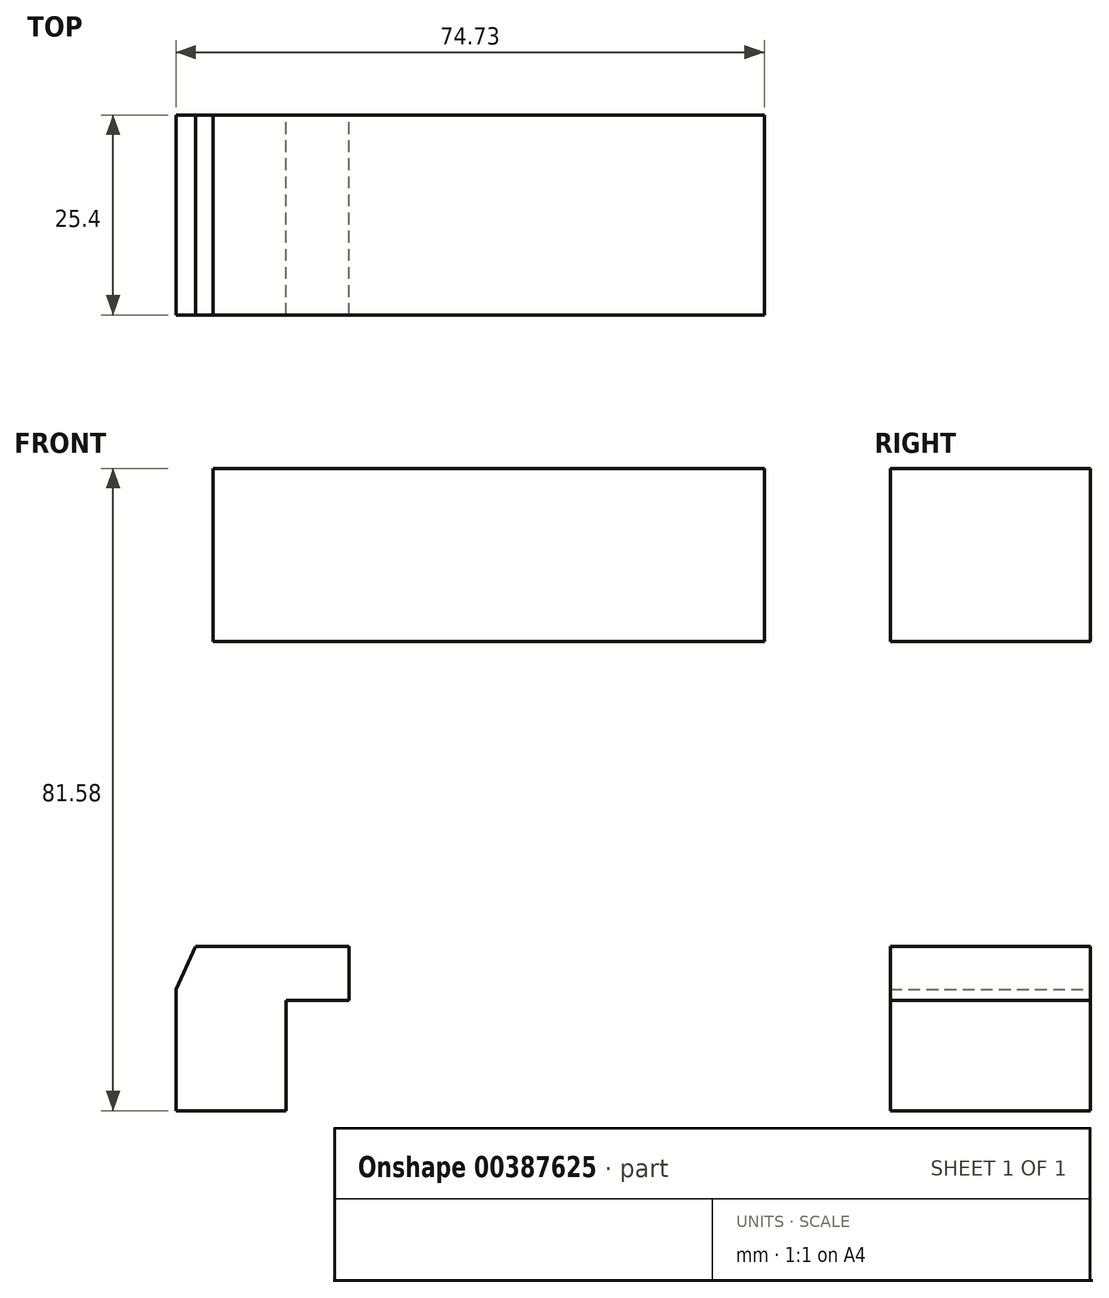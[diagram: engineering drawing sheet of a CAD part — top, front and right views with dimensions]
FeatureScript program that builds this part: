
annotation { "Feature Type Name" : "Feature", "Feature Type Description" : "" }
export const myFeature = defineFeature(function(context is Context, id is Id, definition is map)
    precondition{}
    {
        {
            var Q0;
            Q0=qCreatedBy(makeId("Front.planeOp"),FACE);
            var sketch = newSketch(context, id + "F0", { "sketchPlane" : qUnion([Q0])});
            skLineSegment(sketch, "E0.bottom", {"start": v(-36.75, 49.3) * mm, "end": v(33.26, 49.3) * mm});
            skLineSegment(sketch, "E0.top", {"start": v(-36.75, 27.3) * mm, "end": v(33.26, 27.3) * mm});
            skLineSegment(sketch, "E0.left", {"start": v(-36.75, 49.3) * mm, "end": v(-36.75, 27.3) * mm});
            skLineSegment(sketch, "E0.right", {"start": v(33.26, 49.3) * mm, "end": v(33.26, 27.3) * mm});
            skLineSegment(sketch, "E1.left", {"start": v(-36.75, 49.3) * mm, "end": v(-36.75, 38.3) * mm});
            skLineSegment(sketch, "E1.right", {"start": v(33.26, 49.3) * mm, "end": v(33.26, 38.3) * mm});
            skLineSegment(sketch, "E2", {"start": v(-41.47, -16.9) * mm, "end": v(-41.47, -32.29) * mm});
            skLineSegment(sketch, "E3", {"start": v(-27.48, -32.29) * mm, "end": v(-41.47, -32.29) * mm});
            skLineSegment(sketch, "E4", {"start": v(-27.48, -32.29) * mm, "end": v(-27.48, -18.29) * mm});
            skLineSegment(sketch, "E5", {"start": v(-27.48, -18.29) * mm, "end": v(-19.48, -18.29) * mm});
            skLineSegment(sketch, "E6", {"start": v(-19.48, -18.29) * mm, "end": v(-19.48, -11.4) * mm});
            skLineSegment(sketch, "E7", {"start": v(-19.48, -11.4) * mm, "end": v(-39, -11.4) * mm});
            skLineSegment(sketch, "E8", {"start": v(-39, -11.4) * mm, "end": v(-41.47, -16.9) * mm});
            skLineSegment(sketch, "E9", {"start": v(-36.75, 38.3) * mm, "end": v(33.26, 38.3) * mm});
            skSolve(sketch);
        }
        {
            var Q0;
            Q0 = qSketchRegion(id + "F0", true);
            extrude(context, id + "F1", {"entities" : qUnion([Q0]), "depth" : 25.4 * mm});
        }
    });
